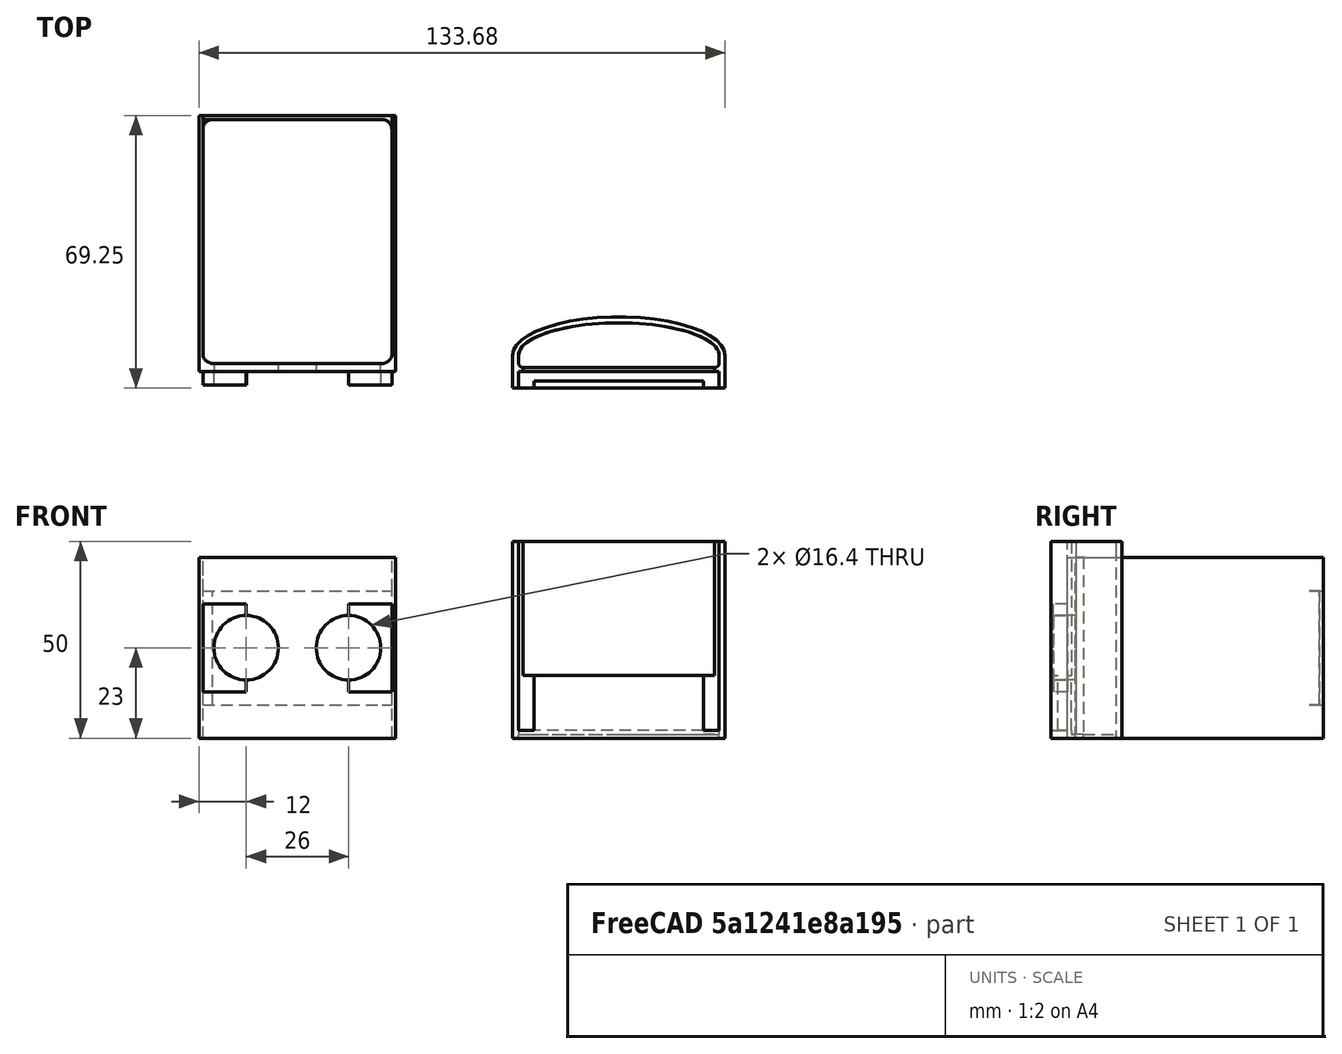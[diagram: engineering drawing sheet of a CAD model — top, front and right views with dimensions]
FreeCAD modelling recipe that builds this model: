
FCSTD DOCUMENT  (FreeCAD 0.18.4R)
Label: sonic.sensor
License: All rights reserved
LicenseURL: http://en.wikipedia.org/wiki/All_rights_reserved
objects: Part::Extrusion×19, Part::Feature×19, Part::Part2DObjectPython×13, Part::Cut×11, Part::MultiFuse×8, Part::FeaturePython×4, Part::Box×2, App::DocumentObjectGroup×1
note: 76 computed .brp shape members not serialized (recipe doc carries the construction recipe); baked Part::Feature solids carry a one-line shape summary decoded from their .brp

FEATURE [Part::Box] Box  label="Cube"
  AttacherType = Attacher::AttachEngine3D
  Height = 46
  Length = 50
  Width = 2
FEATURE [Part::Box] Box001  label="Cube001"
  AttacherType = Attacher::AttachEngine3D
  Height = 46
  Length = 1
  Width = 35
FEATURE [Part::Part2DObjectPython] Circle  label="Circle002"  # Draft 2D object (typed FeaturePython)
  FirstAngle = 0
  LastAngle = 0
  MakeFace = true
  Placement = pos=(12,0,23) rot=(0,0.707107,-0.707107;3.14159rad)
  Radius = 8
FEATURE [Part::Part2DObjectPython] Circle002  label="Circle003"  # Draft 2D object (typed FeaturePython)
  FirstAngle = 0
  LastAngle = 0
  MakeFace = true
  Placement = pos=(38,0,23) rot=(0,0.707107,-0.707107;3.14159rad)
  Radius = 8
FEATURE [Part::Extrusion] Extrusion
  Base = -> Circle
  Dir = (0,11,2.4e-15)
  DirMode = 0
  FaceMakerClass = Part::FaceMakerBullseye
  LengthFwd = 0
  LengthRev = 0
  Solid = true
  Symmetric = false
FEATURE [Part::Extrusion] Extrusion001
  Base = -> Circle002
  Dir = (0,11,2.4e-15)
  DirMode = 0
  FaceMakerClass = Part::FaceMakerBullseye
  LengthFwd = 0
  LengthRev = 0
  Solid = true
  Symmetric = false
FEATURE [Part::Cut] Cut
  Base = -> Box
  Tool = -> Extrusion
FEATURE [Part::Cut] Cut001
  Base = -> Cut
  Tool = -> Extrusion001
FEATURE [Part::Feature] Box002  label="Cube002"
  Placement = pos=(49,0,0) rot=(0,0,1;0rad)
  shape: bbox 1 x 35 x 46 mm, 6 faces (baked)
FEATURE [Part::Feature] Box005  label="Cube005"
  Placement = pos=(0,33,8.5) rot=(0,0,1;0rad)
  shape: bbox 50 x 2 x 29 mm, 6 faces (baked)
FEATURE [Part::MultiFuse] Fusion
  Shapes = -> [Box005,Box002,Cut001,Box001]
FEATURE [Part::Part2DObjectPython] Rectangle001  # Draft 2D object (typed FeaturePython)
  ChamferSize = 0
  Columns = 1
  FilletRadius = 0
  Height = 173.173
  Length = 199.693
  MakeFace = true
  Placement = pos=(-99.8466,18.5,-3.6e-15) rot=(1,0,0;1.5708rad)
  Rows = 1
  Support = -> [Fusion]
FEATURE [Part::FeaturePython] Slice  # WARN: FeaturePython — macro-defined, semantics opaque (R4)
  Base = -> Fusion
  Mode = 1
  Tolerance = 0
  Tools = -> [Rectangle001]
FEATURE [App::DocumentObjectGroup] GrExplode_Slice  label="Exploded Slice"
FEATURE [Part::FeaturePython] Slice_child0  label="Slice.0"  # WARN: FeaturePython — macro-defined, semantics opaque (R4)
  Base = -> Slice
  FilterType = 1
  Invert = false
  OverrideMaxVal = 0
  WindowFrom = 80
  WindowTo = 100
  items = 0
FEATURE [Part::Feature] Slice_child  label="Slice.002"
  Placement = pos=(0,-30,0) rot=(0,0,1;0rad)
  shape: bbox 50 x 18.5 x 46 mm, 24 faces (baked)
FEATURE [Part::Feature] Face
  shape: bbox 1 x 3e-07 x 46 mm, 1 faces, 0 solids (baked)
FEATURE [Part::Extrusion] Extrusion002
  Base = -> Face
  Dir = (-9e-16,-30,6.7e-15)
  DirMode = 0
  FaceMakerClass = Part::FaceMakerBullseye
  LengthFwd = 0
  LengthRev = 0
  Solid = true
  Symmetric = false
FEATURE [Part::Feature] Face001
  shape: bbox 1 x 3e-07 x 46 mm, 1 faces, 0 solids (baked)
FEATURE [Part::Extrusion] Extrusion003
  Base = -> Face001
  Dir = (-9e-16,-30,6.7e-15)
  DirMode = 0
  FaceMakerClass = Part::FaceMakerBullseye
  LengthFwd = 0
  LengthRev = 0
  Solid = true
  Symmetric = false
FEATURE [Part::MultiFuse] Fusion001
  Shapes = -> [Slice_child,Extrusion002,Extrusion003]
FEATURE [Part::MultiFuse] Fusion002
  Shapes = -> [Fusion001,Slice_child0]
FEATURE [Part::Part2DObjectPython] Circle003  label="Circle004"  # Draft 2D object (typed FeaturePython)
  FirstAngle = 0
  LastAngle = 0
  MakeFace = true
  Placement = pos=(12,-30,23) rot=(1,0,0;1.5708rad)
  Radius = 8.2
FEATURE [Part::Part2DObjectPython] Circle004  label="Circle005"  # Draft 2D object (typed FeaturePython)
  FirstAngle = 0
  LastAngle = 0
  MakeFace = true
  Placement = pos=(38,-30,23) rot=(1,0,0;1.5708rad)
  Radius = 8.2
FEATURE [Part::Extrusion] Extrusion004
  Base = -> Circle003
  Dir = (1e-16,2,-4e-16)
  DirMode = 0
  FaceMakerClass = Part::FaceMakerBullseye
  LengthFwd = 0
  LengthRev = 0
  Solid = true
  Symmetric = false
FEATURE [Part::Extrusion] Extrusion005
  Base = -> Circle004
  Dir = (1e-16,2,-4e-16)
  DirMode = 0
  FaceMakerClass = Part::FaceMakerBullseye
  LengthFwd = 0
  LengthRev = 0
  Solid = true
  Symmetric = false
FEATURE [Part::Cut] Cut002
  Base = -> Fusion002
  Tool = -> Extrusion004
FEATURE [Part::Cut] Cut003
  Base = -> Cut002
  Tool = -> Extrusion005
FEATURE [Part::Feature] Face002
  shape: bbox 48 x 3e-07 x 29 mm, 1 faces, 0 solids (baked)
FEATURE [Part::Extrusion] Extrusion006
  Base = -> Face002
  Dir = (0,1,0)
  DirMode = 0
  FaceMakerClass = Part::FaceMakerBullseye
  LengthFwd = 0
  LengthRev = 0
  Solid = true
  Symmetric = false
FEATURE [Part::Cut] Cut004
  Base = -> Cut003
  Tool = -> Extrusion006
FEATURE [Part::Part2DObjectPython] Rectangle  # Draft 2D object (typed FeaturePython)
  ChamferSize = 0
  Columns = 1
  FilletRadius = 0
  Height = 2.5
  Length = 2.5
  MakeFace = true
  Placement = pos=(46.5472,-28,0) rot=(0.707107,0.707107,0;3.14159rad)
  Rows = 1
  Support = -> [Cut004]
FEATURE [Part::Extrusion] Extrusion007
  Base = -> Rectangle
  Dir = (0,0,46)
  DirMode = 0
  FaceMakerClass = Part::FaceMakerBullseye
  LengthFwd = 0
  LengthRev = 0
  Solid = true
  Symmetric = false
FEATURE [Part::Part2DObjectPython] Circle005  label="Circle006"  # Draft 2D object (typed FeaturePython)
  FirstAngle = 0
  LastAngle = 0
  MakeFace = true
  Placement = pos=(46.5472,-25.5,0) rot=(0.707107,0.707107,0;3.14159rad)
  Radius = 2.5
  Support = -> [Extrusion007]
FEATURE [Part::Extrusion] Extrusion008
  Base = -> Circle005
  Dir = (0,0,46)
  DirMode = 0
  FaceMakerClass = Part::FaceMakerBullseye
  LengthFwd = 0
  LengthRev = 0
  Solid = true
  Symmetric = false
FEATURE [Part::Feature] Extrusion009
  Placement = pos=(-45.5472,0,0) rot=(0,0,1;0rad)
  shape: bbox 2.5 x 2.5 x 46 mm, 6 faces (baked)
FEATURE [Part::Feature] Extrusion010
  Placement = pos=(-43.0472,0,0) rot=(0,0,1;0rad)
  shape: bbox 5 x 5 x 46 mm, 3 faces (baked)
FEATURE [Part::Cut] Cut005
  Base = -> Extrusion007
  Tool = -> Extrusion008
FEATURE [Part::Cut] Cut006
  Base = -> Extrusion009
  Tool = -> Extrusion010
FEATURE [Part::MultiFuse] Fusion003
  Shapes = -> [Cut004,Cut006,Cut005]
FEATURE [Part::Part2DObjectPython] Rectangle002  # Draft 2D object (typed FeaturePython)
  ChamferSize = 0
  Columns = 1
  FilletRadius = 0
  Height = 2.5
  Length = 2.5
  MakeFace = true
  Placement = pos=(1,31.4564,8.5) rot=(0.707107,0.707107,0;3.14159rad)
  Rows = 1
  Support = -> [Fusion003]
FEATURE [Part::Extrusion] Extrusion011
  Base = -> Rectangle002
  Dir = (0,0,29)
  DirMode = 0
  FaceMakerClass = Part::FaceMakerBullseye
  LengthFwd = 0
  LengthRev = 0
  Solid = true
  Symmetric = false
FEATURE [Part::Feature] Extrusion012
  Placement = pos=(45.5,0.043591,0) rot=(0,0,1;0rad)
  shape: bbox 2.5 x 2.5 x 29 mm, 6 faces (baked)
FEATURE [Part::Part2DObjectPython] Circle006  label="Circle007"  # Draft 2D object (typed FeaturePython)
  FirstAngle = 0
  LastAngle = 0
  MakeFace = true
  Placement = pos=(46.5,31.5,8.5) rot=(0.707107,0.707107,0;3.14159rad)
  Radius = 2.5
  Support = -> [Extrusion012]
FEATURE [Part::Extrusion] Extrusion013
  Base = -> Circle006
  Dir = (0,0,29)
  DirMode = 0
  FaceMakerClass = Part::FaceMakerBullseye
  LengthFwd = 0
  LengthRev = 0
  Solid = true
  Symmetric = false
FEATURE [Part::Feature] Extrusion014
  Placement = pos=(-43,-0.043591,0) rot=(0,0,1;0rad)
  shape: bbox 5 x 5 x 29 mm, 3 faces (baked)
FEATURE [Part::Cut] Cut007
  Base = -> Extrusion011
  Tool = -> Extrusion014
FEATURE [Part::Cut] Cut008
  Base = -> Extrusion012
  Tool = -> Extrusion013
FEATURE [Part::Part2DObjectPython] Rectangle004  # Draft 2D object (typed FeaturePython)
  ChamferSize = 0
  Columns = 1
  FilletRadius = 0
  Height = 16.4
  Length = 11
  MakeFace = true
  Placement = pos=(38,-30,14.8) rot=(1,0,0;1.5708rad)
  Rows = 1
FEATURE [Part::Extrusion] Extrusion018
  Base = -> Rectangle004
  Dir = (-1e-16,-3.5,8e-16)
  DirMode = 0
  FaceMakerClass = Part::FaceMakerBullseye
  LengthFwd = 0
  LengthRev = 0
  Solid = true
  Symmetric = false
FEATURE [Part::Feature] Extrusion019
  Placement = pos=(-36.9432,0,0) rot=(0,0,1;0rad)
  shape: bbox 11 x 3.5 x 16.4 mm, 6 faces (baked)
FEATURE [Part::Part2DObjectPython] Circle007  label="Circle008"  # Draft 2D object (typed FeaturePython)
  FirstAngle = 0
  LastAngle = 0
  MakeFace = true
  Placement = pos=(38,-30,23) rot=(1,0,0;1.5708rad)
  Radius = 8.2
FEATURE [Part::Part2DObjectPython] Circle008  label="Circle009"  # Draft 2D object (typed FeaturePython)
  FirstAngle = 0
  LastAngle = 0
  MakeFace = true
  Placement = pos=(12,-30,23) rot=(1,0,0;1.5708rad)
  Radius = 8.2
FEATURE [Part::Extrusion] Extrusion020
  Base = -> Circle008
  Dir = (-1e-16,-3.5,8e-16)
  DirMode = 0
  FaceMakerClass = Part::FaceMakerBullseye
  LengthFwd = 0
  LengthRev = 0
  Solid = true
  Symmetric = false
FEATURE [Part::Extrusion] Extrusion021
  Base = -> Circle007
  Dir = (-1e-16,-3.5,8e-16)
  DirMode = 0
  FaceMakerClass = Part::FaceMakerBullseye
  LengthFwd = 0
  LengthRev = 0
  Solid = true
  Symmetric = false
FEATURE [Part::Cut] Cut009
  Base = -> Extrusion018
  Tool = -> Extrusion021
FEATURE [Part::Cut] Cut010
  Base = -> Extrusion019
  Tool = -> Extrusion020
FEATURE [Part::Part2DObjectPython] Rectangle005  # Draft 2D object (typed FeaturePython)
  ChamferSize = 0
  Columns = 1
  FilletRadius = 0
  Height = 103.191
  Length = 80.6131
  MakeFace = true
  Placement = pos=(-16.8842,-30,-30.2506) rot=(1,0,0;1.5708rad)
  Rows = 1
FEATURE [Part::FeaturePython] Slice001  # WARN: FeaturePython — macro-defined, semantics opaque (R4)
  Base = -> Fusion003
  Mode = 1
  Tolerance = 0
  Tools = -> [Rectangle005]
FEATURE [Part::FeaturePython] Slice001_child0  label="Slice001.0"  # WARN: FeaturePython — macro-defined, semantics opaque (R4)
  Base = -> Slice001
  FilterType = 1
  Invert = false
  OverrideMaxVal = 0
  WindowFrom = 80
  WindowTo = 100
  items = 0
FEATURE [Part::MultiFuse] Fusion020
  Shapes = -> [Cut007,Cut008,Slice001_child0]
FEATURE [Part::MultiFuse] Fusion022
  Shapes = -> [Fusion020,Cut010,Cut009]
FEATURE [Part::Feature] Fusion023
  Placement = pos=(81.6551,-60.2333,48) rot=(1,0,0;3.14159rad)
  shape: bbox 54 x 18.07 x 50 mm, 95 faces (baked)
FEATURE [Part::Feature] Face003
  Placement = pos=(81.6551,-60.2333,48) rot=(1,0,0;3.14159rad)
  shape: bbox 43.05 x 2e-07 x 14 mm, 1 faces, 0 solids (baked)
FEATURE [Part::Extrusion] Extrusion022
  Base = -> Face003
  Dir = (0,-0.816665,6e-16)
  DirMode = 0
  FaceMakerClass = Part::FaceMakerBullseye
  LengthFwd = 0
  LengthRev = 0
  Solid = true
  Symmetric = false
FEATURE [Part::MultiFuse] Fusion024
  Shapes = -> [Extrusion022,Fusion023]
FEATURE [Part::Feature] Fusion024001  label="Fusion025"
  shape: bbox 54 x 18.07 x 50 mm, 97 faces (baked)
FEATURE [Part::Feature] Fusion024001_solid  label="Fusion025 (Solid)"
  shape: bbox 54 x 18.07 x 50 mm, 97 faces (baked)
FEATURE [Part::Feature] Face009
  shape: bbox 10.94 x 3.5 x 2e-07 mm, 1 faces, 0 solids (baked)
FEATURE [Part::Extrusion] Extrusion023
  Base = -> Face009
  Dir = (-1e-16,7e-16,3)
  DirMode = 0
  FaceMakerClass = Part::FaceMakerBullseye
  LengthFwd = 0
  LengthRev = 0
  Solid = true
  Symmetric = false
FEATURE [Part::Feature] Face010
  shape: bbox 11 x 3.5 x 2e-07 mm, 1 faces, 0 solids (baked)
FEATURE [Part::Extrusion] Extrusion024
  Base = -> Face010
  Dir = (-1e-16,7e-16,3)
  DirMode = 0
  FaceMakerClass = Part::FaceMakerBullseye
  LengthFwd = 0
  LengthRev = 0
  Solid = true
  Symmetric = false
FEATURE [Part::Feature] Face011
  shape: bbox 10.94 x 3.5 x 2e-07 mm, 1 faces, 0 solids (baked)
FEATURE [Part::Extrusion] Extrusion025
  Base = -> Face011
  Dir = (1e-16,-7e-16,-2.9998)
  DirMode = 0
  FaceMakerClass = Part::FaceMakerBullseye
  LengthFwd = 0
  LengthRev = 0
  Solid = true
  Symmetric = false
FEATURE [Part::Feature] Face012
  shape: bbox 11 x 3.5 x 2e-07 mm, 1 faces, 0 solids (baked)
FEATURE [Part::Extrusion] Extrusion026
  Base = -> Face012
  Dir = (1e-16,-7e-16,-2.9998)
  DirMode = 0
  FaceMakerClass = Part::FaceMakerBullseye
  LengthFwd = 0
  LengthRev = 0
  Solid = true
  Symmetric = false
FEATURE [Part::MultiFuse] Fusion024002
  Shapes = -> [Fusion022,Extrusion023,Extrusion025,Extrusion024,Extrusion026]
